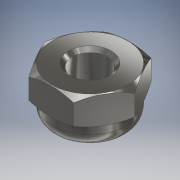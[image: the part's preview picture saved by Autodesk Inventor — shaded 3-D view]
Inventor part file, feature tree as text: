
AUTODESK INVENTOR PART (.ipt)
format: ipt  version: 2019 (Build 230136000, 136)  size: 203,776 bytes
history: native  units: mm
features: sketch x4, extrude x3, fillet x2, other x1, revolve x1, chamfer x1
ambient origin geometry x8: Origin, YZ Plane, XZ Plane, XY Plane, X Axis, Y Axis, Z Axis, Center Point
bodies: Body1 (feature_tree)
feature tree (12):
  other  "Твердое тело1"
  extrude  "Выдавливание1"  Depth=4.0mm TaperAngle=0.0deg
  revolve  "Вращение1"
  extrude  "Выдавливание2"  TaperAngle=60.0deg  [1 undecoded]
  fillet  "Сопряжение1"  Radius=1.0mm
  chamfer  "Фаска2"  Distance=3.5mm
  extrude  "Extrusion4"  TaperAngle=90.0deg  [1 undecoded]
  fillet  "Fillet3"  Radius=3.0mm
  sketch  "Эскиз1"
  sketch  "Эскиз2"
  sketch  "Эскиз3"
  sketch  "Sketch5"  dims[d0=5.0mm d2=4.0mm d3=0.0mm d4=60.0deg d5=1.0mm d6=3.5mm d7=90.0deg d8=3.0mm d9=0.0mm d10=2.0mm d18=0.5mm d19=2.0mm d20=45.0deg d21=3.0mm d22=0.2mm d23=0.0mm d24=0.2mm]
note: 2 required parameter values undecoded (feature->parameter linkage not recoverable at this tier; creation-order binding heuristic only, values carry confidence <= 0.55)
